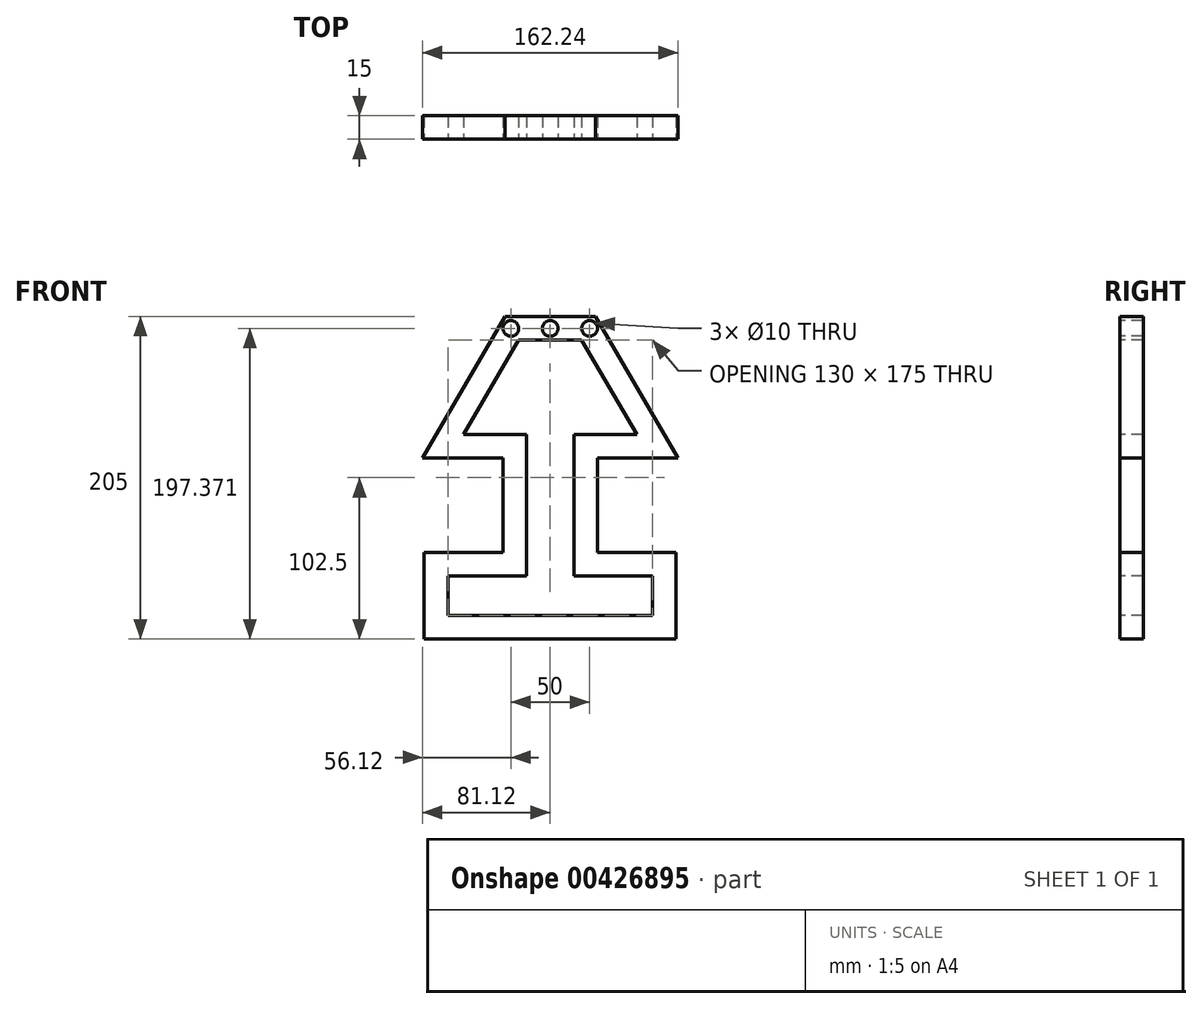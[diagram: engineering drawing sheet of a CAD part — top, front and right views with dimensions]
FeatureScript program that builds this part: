
annotation { "Feature Type Name" : "Feature", "Feature Type Description" : "" }
export const myFeature = defineFeature(function(context is Context, id is Id, definition is map)
    precondition{}
    {
        {
            var Q0;
            Q0=qCreatedBy(makeId("Front.planeOp"),FACE);
            var sketch = newSketch(context, id + "F0", { "sketchPlane" : qUnion([Q0])});
            skLineSegment(sketch, "E0", {"start": v(-20, 60) * mm, "end": v(-55, 0) * mm});
            skLineSegment(sketch, "E1", {"start": v(-65, -90) * mm, "end": v(-15, -90) * mm});
            skLineSegment(sketch, "E2.MirrorCS", {"start": v(-15, 0) * mm, "end": v(-15, -90) * mm});
            skLineSegment(sketch, "E3.MirrorCS", {"start": v(15, 0) * mm, "end": v(15, -90) * mm});
            skLineSegment(sketch, "E4", {"start": v(20, 60) * mm, "end": v(-20, 60) * mm});
            skLineSegment(sketch, "E5", {"start": v(20, 60) * mm, "end": v(55, 0) * mm});
            skLineSegment(sketch, "E6", {"start": v(-65, -90) * mm, "end": v(-65, -115) * mm});
            skLineSegment(sketch, "E7", {"start": v(65, -115) * mm, "end": v(65, -90) * mm});
            skLineSegment(sketch, "E8", {"start": v(65, -90) * mm, "end": v(15, -90) * mm});
            skLineSegment(sketch, "E9", {"start": v(-65, -115) * mm, "end": v(65, -115) * mm});
            skLineSegment(sketch, "E10", {"start": v(-15, 0) * mm, "end": v(-55, 0) * mm});
            skLineSegment(sketch, "E11", {"start": v(15, 0) * mm, "end": v(55, 0) * mm});
            skSolve(sketch);
        }
        {
            var Q0;
            Q0=qCreatedBy(makeId("Front.planeOp"),FACE);
            var sketch = newSketch(context, id + "F1", { "sketchPlane" : qUnion([Q0])});
            skLineSegment(sketch, "E12", {"start": v(-80, -75) * mm, "end": v(-30, -75) * mm});
            skLineSegment(sketch, "E13.MirrorCS", {"start": v(30, -15) * mm, "end": v(30, -75) * mm});
            skLineSegment(sketch, "E14.MirrorCS", {"start": v(80, -130) * mm, "end": v(80, -75) * mm});
            skLineSegment(sketch, "E15.MirrorCS", {"start": v(80, -75) * mm, "end": v(30, -75) * mm});
            skLineSegment(sketch, "E16", {"start": v(-80, -130) * mm, "end": v(80, -130) * mm});
            skLineSegment(sketch, "E17", {"start": v(30, -15) * mm, "end": v(81.12, -15) * mm});
            skLineSegment(sketch, "E18", {"start": v(81.12, -15) * mm, "end": v(28.62, 75) * mm});
            skLineSegment(sketch, "E19", {"start": v(-80, -75) * mm, "end": v(-80, -130) * mm});
            skLineSegment(sketch, "E20", {"start": v(-30, -15) * mm, "end": v(-30, -75) * mm});
            skLineSegment(sketch, "E21", {"start": v(28.62, 75) * mm, "end": v(-28.62, 75) * mm});
            skLineSegment(sketch, "E22", {"start": v(-28.62, 75) * mm, "end": v(-81.12, -15) * mm});
            skLineSegment(sketch, "E23", {"start": v(-81.12, -15) * mm, "end": v(-30, -15) * mm});
            skCircle(sketch, "E24", {"center": v(0, 67.37) * mm, "radius": 5 * mm});
            skCircle(sketch, "E25.1.0.0", {"center": v(25, 67.37) * mm, "radius": 5 * mm});
            skLineSegment(sketch, "E25.direction1", {"start": v(0, 67.37) * mm, "end": v(25, 67.37) * mm, "construction": true});
            skCircle(sketch, "E26.1.0.0", {"center": v(-25, 67.37) * mm, "radius": 5 * mm});
            skLineSegment(sketch, "E26.direction1", {"start": v(0, 67.37) * mm, "end": v(-25, 67.37) * mm, "construction": true});
            skSolve(sketch);
        }
        {
            var Q0;
            Q0=makeQuery(id+"F1.imprint","IMPRINT",FACE,{"disambiguationData":[TD([[makeQuery(id+"F1.imprint","IMPRINT",EDGE,{"derivedFrom":sQuery(id+"F1.wireOp",EDGE,"E12")}),-1.0]])]});
            var Q1;
            Q1 = qConstructionFilter(qBodyType(qCreatedBy(id + "F1" ,EDGE), BodyType.WIRE), ConstructionObject.NO);
            extrude(context, id + "F2", {"entities" : qUnion([Q0]), "surfaceEntities" : qUnion([Q1]), "oppositeDirection" : true, "depth" : 15 * mm, "offsetDistance" : 25 * mm});
        }
        {
            var Q0;
            Q0 = qSketchRegion(id + "F0", true);
            extrude(context, id + "F3", {"entities" : qUnion([Q0]), "operationType" : NewBodyOperationType.REMOVE, "endBound" : BoundingType.THROUGH_ALL, "oppositeDirection" : true, "depth" : 25 * mm, "offsetDistance" : 25 * mm});
        }
    });
